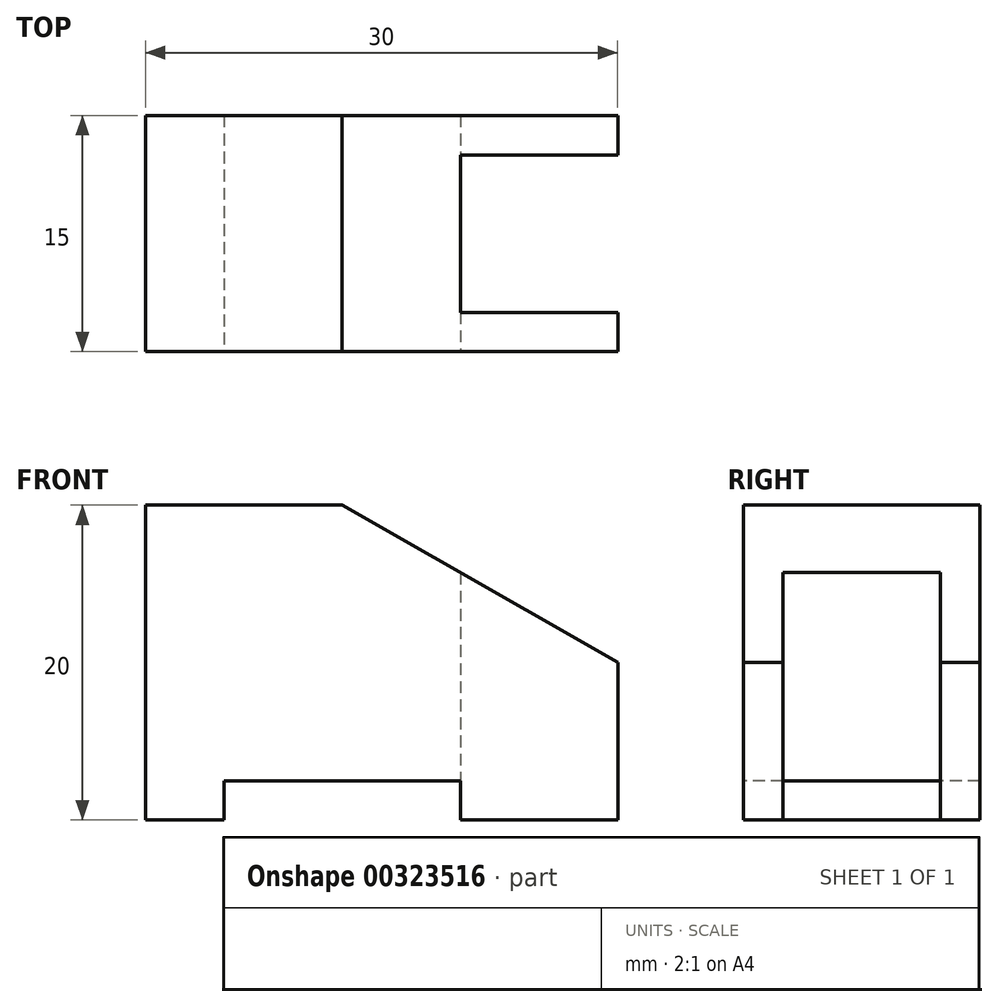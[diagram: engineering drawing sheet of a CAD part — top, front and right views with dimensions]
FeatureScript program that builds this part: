
annotation { "Feature Type Name" : "Feature", "Feature Type Description" : "" }
export const myFeature = defineFeature(function(context is Context, id is Id, definition is map)
    precondition{}
    {
        {
            var Q0;
            Q0=qCreatedBy(makeId("Front.planeOp"),FACE);
            var sketch = newSketch(context, id + "F0", { "sketchPlane" : qUnion([Q0])});
            skLineSegment(sketch, "E0", {"start": v(-29.05, 24.2) * mm, "end": v(-29.05, 4.2) * mm});
            skLineSegment(sketch, "E1", {"start": v(-29.05, 4.2) * mm, "end": v(-24.05, 4.2) * mm});
            skLineSegment(sketch, "E2", {"start": v(-24.05, 4.2) * mm, "end": v(-24.05, 6.7) * mm});
            skLineSegment(sketch, "E3", {"start": v(-24.05, 6.7) * mm, "end": v(-9.05, 6.7) * mm});
            skLineSegment(sketch, "E4", {"start": v(-9.05, 6.7) * mm, "end": v(-9.05, 4.2) * mm});
            skLineSegment(sketch, "E5", {"start": v(-9.05, 4.2) * mm, "end": v(0.95, 4.2) * mm});
            skLineSegment(sketch, "E6", {"start": v(0.95, 4.2) * mm, "end": v(0.95, 14.2) * mm});
            skLineSegment(sketch, "E7", {"start": v(-29.05, 24.2) * mm, "end": v(-16.55, 24.2) * mm});
            skLineSegment(sketch, "E8", {"start": v(-16.55, 24.2) * mm, "end": v(0.95, 14.2) * mm});
            skSolve(sketch);
        }
        {
            var Q0;
            Q0 = qSketchRegion(id + "F0", true);
            extrude(context, id + "F1", {"entities" : qUnion([Q0]), "oppositeDirection" : true, "depth" : 15 * mm});
        }
        {
            var Q0;
            Q0=makeQuery(id+"F1.opExtrude","SWEPT_FACE",FACE,{"disambiguationData":[OSD([sQuery(id+"F0.wireOp",EDGE,"E5")])]});
            var sketch = newSketch(context, id + "F2", { "sketchPlane" : qUnion([Q0])});
            skLineSegment(sketch, "E9", {"start": v(0.95, -7.5) * mm, "end": v(0.95, -2.5) * mm});
            skLineSegment(sketch, "E10", {"start": v(0.95, -2.5) * mm, "end": v(-9.05, -2.5) * mm});
            skLineSegment(sketch, "E11", {"start": v(-9.05, -2.5) * mm, "end": v(-9.05, -12.5) * mm});
            skLineSegment(sketch, "E12", {"start": v(-9.05, -12.5) * mm, "end": v(0.95, -12.5) * mm});
            skLineSegment(sketch, "E13", {"start": v(0.95, -12.5) * mm, "end": v(0.95, -7.5) * mm});
            skSolve(sketch);
        }
        {
            var Q0;
            Q0 = qSketchRegion(id + "F2", true);
            extrude(context, id + "F3", {"entities" : qUnion([Q0]), "operationType" : NewBodyOperationType.REMOVE, "oppositeDirection" : true, "depth" : 25 * mm});
        }
    });
